# Revit family: РИДАН_Соленоидный клапан EV220WR
name_source: partatom
category: Арматура трубопроводов
units: mm (PartAtom-declared; Revit-internal decimal feet)

## family parameters
Всегда вертикально = Да
На основе рабочей плоскости = Нет
Общий = Нет
При загрузке вырезать с полостями = Нет
Размер круглого соединителя = Использовать диаметр
Тип детали = Вставляется

## types (84) — shared parameters
ADSK_Единица измерения = шт.
ADSK_Завод-изготовитель = ООО «Ридан-Трейд»
ADSK_Классификация нагрузок = Прочее
ADSK_Количество = 1
ADSK_Количество фаз = 1
ADSK_Коэффициент мощности = 1
ADSK_Потеря давления жидкости = 0.0 Па
ADSK_Расход жидкости = 0.0 л/с
LT = EV220WR _DN10_50
Table = EV220WR _DN10_50_1
angle1 = 150.00°
h2 = 69 мм

## per-type parameters (varying)
- EV220WR НЗ EPDM 0,3-16 бар 230 В 50 Гц DN10: ADSK_Диаметр условный=10 мм; ADSK_Код изделия=042U001031R; ADSK_Марка=EV220WR DN10; ADSK_Масса=0.7; ADSK_Наименование=Клапан электромагнитный EV220WR, нормально закрытый, EPDM, 0,3-16 бар, 230 В, 50 Гц, DN10; ADSK_Напряжение=230 В; ADSK_Номинальная мощность=22 Вт; ADSK_Полная мощность=22 В·А; ADSK_Пропускная способность=1.1 л/с; a=15 мм; b=15 мм; c=26 мм; d=15 мм; e=18 мм; f=36 мм; g=12 мм; h=24 мм; h1=12 мм; i=48 мм; j=4 мм; k=23 мм; l=11 мм; m=28 мм; n=16 мм; o=9 мм; p=28 мм; p1=2 мм; r=1 мм; r1=1 мм; r2=2 мм; s=38 мм; t=15 мм; t1=1 мм; u=15 мм; u1=9 мм; v=17 мм; w=77 мм; x=36 мм; x1=39 мм; x2=4 мм; x3=5 мм; y=48 мм; Ду10_40=Да; Ду50=Нет
- EV220WR НЗ EPDM 0,3-16 бар 230 В 50 Гц DN15: ADSK_Диаметр условный=15 мм; ADSK_Код изделия=042U001531R; ADSK_Марка=EV220WR DN15; ADSK_Масса=0.7; ADSK_Наименование=Клапан электромагнитный EV220WR, нормально закрытый, EPDM, 0,3-16 бар, 230 В, 50 Гц, DN15; ADSK_Напряжение=230 В; ADSK_Номинальная мощность=22 Вт; ADSK_Полная мощность=22 В·А; ADSK_Пропускная способность=1.1 л/с; a=15 мм; b=15 мм; c=26 мм; d=15 мм; e=18 мм; f=36 мм; g=12 мм; h=24 мм; h1=12 мм; i=48 мм; j=4 мм; k=23 мм; l=11 мм; m=28 мм; n=16 мм; o=9 мм; p=28 мм; p1=2 мм; r=1 мм; r1=1 мм; r2=2 мм; s=38 мм; t=15 мм; t1=1 мм; u=15 мм; u1=9 мм; v=17 мм; w=77 мм; x=36 мм; x1=39 мм; x2=4 мм; x3=5 мм; y=48 мм; Ду10_40=Да; Ду50=Нет
- EV220WR НЗ EPDM 0,3-16 бар 230 В 50 Гц DN20: ADSK_Диаметр условный=20 мм; ADSK_Код изделия=042U002031R; ADSK_Марка=EV220WR DN20; ADSK_Масса=0.85; ADSK_Наименование=Клапан электромагнитный EV220WR, нормально закрытый, EPDM, 0,3-16 бар, 230 В, 50 Гц, DN20; ADSK_Напряжение=230 В; ADSK_Номинальная мощность=22 Вт; ADSK_Полная мощность=22 В·А; ADSK_Пропускная способность=1.9 л/с; a=16 мм; b=18 мм; c=31 мм; d=20 мм; e=18 мм; f=35 мм; g=15 мм; h=29 мм; h1=14 мм; i=57 мм; j=5 мм; k=24 мм; l=11 мм; m=32 мм; n=21 мм; o=10 мм; p=30 мм; p1=2 мм; r=2 мм; r1=2 мм; r2=2 мм; s=39 мм; t=20 мм; t1=2 мм; u=24 мм; u1=9 мм; v=18 мм; w=78 мм; x=43 мм; x1=43 мм; x2=5 мм; x3=7 мм; y=57 мм; Ду10_40=Да; Ду50=Нет
- EV220WR НЗ EPDM 0,3-16 бар 230 В 50 Гц DN25: ADSK_Диаметр условный=25 мм; ADSK_Код изделия=042U002531R; ADSK_Марка=EV220WR DN25; ADSK_Масса=1.35; ADSK_Наименование=Клапан электромагнитный EV220WR, нормально закрытый, EPDM, 0,3-16 бар, 230 В, 50 Гц, DN25; ADSK_Напряжение=230 В; ADSK_Номинальная мощность=22 Вт; ADSK_Полная мощность=22 В·А; ADSK_Пропускная способность=2.8 л/с; a=23 мм; b=23 мм; c=41 мм; d=17 мм; e=31 мм; f=62 мм; g=21 мм; h=33 мм; h1=16 мм; i=70 мм; j=8 мм; k=33 мм; l=17 мм; m=40 мм; n=27 мм; o=16 мм; p=30 мм; p1=3 мм; r=13 мм; r1=2 мм; r2=3 мм; s=47 мм; t=25 мм; t1=3 мм; u=29 мм; u1=13 мм; v=28 мм; w=88 мм; x=55 мм; x1=55 мм; x2=6 мм; x3=10 мм; y=70 мм; Ду10_40=Да; Ду50=Нет
- EV220WR НЗ EPDM 0,3-16 бар 230 В 50 Гц DN32: ADSK_Диаметр условный=32 мм; ADSK_Код изделия=042U003231R; ADSK_Марка=EV220WR DN32; ADSK_Масса=2.8; ADSK_Наименование=Клапан электромагнитный EV220WR, нормально закрытый, EPDM, 0,3-16 бар, 230 В, 50 Гц, DN32; ADSK_Напряжение=230 В; ADSK_Номинальная мощность=22 Вт; ADSK_Полная мощность=22 В·А; ADSK_Пропускная способность=5.8 л/с; a=32 мм; b=31 мм; c=57 мм; d=24 мм; e=41 мм; f=83 мм; g=29 мм; h=53 мм; h1=26 мм; i=96 мм; j=12 мм; k=44 мм; l=26 мм; m=52 мм; n=40 мм; o=25 мм; p=31 мм; p1=2 мм; r=22 мм; r1=3 мм; r2=6 мм; s=59 мм; t=35 мм; t1=4 мм; u=39 мм; u1=18 мм; v=38 мм; w=98 мм; x=73 мм; x1=73 мм; x2=6 мм; x3=8 мм; y=96 мм; Ду10_40=Да; Ду50=Нет
- EV220WR НЗ EPDM 0,3-16 бар 230 В 50 Гц DN40: ADSK_Диаметр условный=40 мм; ADSK_Код изделия=042U004031R; ADSK_Марка=EV220WR DN40; ADSK_Масса=2.8; ADSK_Наименование=Клапан электромагнитный EV220WR, нормально закрытый, EPDM, 0,3-16 бар, 230 В, 50 Гц, DN40; ADSK_Напряжение=230 В; ADSK_Номинальная мощность=22 Вт; ADSK_Полная мощность=22 В·А; ADSK_Пропускная способность=7.2 л/с; a=32 мм; b=31 мм; c=57 мм; d=24 мм; e=41 мм; f=83 мм; g=29 мм; h=53 мм; h1=26 мм; i=96 мм; j=12 мм; k=44 мм; l=26 мм; m=52 мм; n=40 мм; o=25 мм; p=31 мм; p1=2 мм; r=22 мм; r1=3 мм; r2=6 мм; s=59 мм; t=35 мм; t1=4 мм; u=39 мм; u1=18 мм; v=38 мм; w=98 мм; x=73 мм; x1=73 мм; x2=6 мм; x3=8 мм; y=96 мм; Ду10_40=Да; Ду50=Нет
- EV220WR НЗ EPDM 0,3-16 бар 230 В 50 Гц DN50: ADSK_Диаметр условный=50 мм; ADSK_Код изделия=042U005031R; ADSK_Марка=EV220WR DN50; ADSK_Масса=3.9; ADSK_Наименование=Клапан электромагнитный EV220WR, нормально закрытый, EPDM, 0,3-16 бар, 230 В, 50 Гц, DN50; ADSK_Напряжение=230 В; ADSK_Номинальная мощность=22 Вт; ADSK_Полная мощность=22 В·А; ADSK_Пропускная способность=11.4 л/с; a=32 мм; b=31 мм; c=57 мм; d=33 мм; e=49 мм; f=99 мм; g=37 мм; h=56 мм; h1=28 мм; i=120 мм; j=15 мм; k=49 мм; l=31 мм; m=60 мм; n=50 мм; o=30 мм; p=40 мм; p1=3 мм; r=27 мм; r1=3 мм; r2=6 мм; s=68 мм; t=40 мм; t1=5 мм; u=39 мм; u1=18 мм; v=48 мм; w=108 мм; x=92 мм; x1=92 мм; x2=8 мм; x3=10 мм; y=130 мм; Ду10_40=Нет; Ду50=Да
- EV220WR НЗ EPDM 0,3-16 бар 24 В пост. Ток DN10: ADSK_Диаметр условный=10 мм; ADSK_Код изделия=042U001002R; ADSK_Марка=EV220WR DN10; ADSK_Масса=0.7; ADSK_Наименование=Клапан электромагнитный EV220WR, нормально закрытый, EPDM, 0,3-16 бар, 24 В пост. Ток, DN10; ADSK_Напряжение=24 В; ADSK_Номинальная мощность=13 Вт; ADSK_Полная мощность=13 В·А; ADSK_Пропускная способность=1.1 л/с; a=15 мм; b=15 мм; c=26 мм; d=15 мм; e=18 мм; f=36 мм; g=12 мм; h=24 мм; h1=12 мм; i=48 мм; j=4 мм; k=23 мм; l=11 мм; m=28 мм; n=16 мм; o=9 мм; p=28 мм; p1=2 мм; r=1 мм; r1=1 мм; r2=2 мм; s=38 мм; t=15 мм; t1=1 мм; u=15 мм; u1=9 мм; v=17 мм; w=77 мм; x=36 мм; x1=39 мм; x2=4 мм; x3=5 мм; y=48 мм; Ду10_40=Да; Ду50=Нет
- EV220WR НЗ EPDM 0,3-16 бар 24 В пост. Ток DN15: ADSK_Диаметр условный=15 мм; ADSK_Код изделия=042U001502R; ADSK_Марка=EV220WR DN15; ADSK_Масса=0.7; ADSK_Наименование=Клапан электромагнитный EV220WR, нормально закрытый, EPDM, 0,3-16 бар, 24 В пост. Ток, DN15; ADSK_Напряжение=24 В; ADSK_Номинальная мощность=13 Вт; ADSK_Полная мощность=13 В·А; ADSK_Пропускная способность=1.1 л/с; a=15 мм; b=15 мм; c=26 мм; d=15 мм; e=18 мм; f=36 мм; g=12 мм; h=24 мм; h1=12 мм; i=48 мм; j=4 мм; k=23 мм; l=11 мм; m=28 мм; n=16 мм; o=9 мм; p=28 мм; p1=2 мм; r=1 мм; r1=1 мм; r2=2 мм; s=38 мм; t=15 мм; t1=1 мм; u=15 мм; u1=9 мм; v=17 мм; w=77 мм; x=36 мм; x1=39 мм; x2=4 мм; x3=5 мм; y=48 мм; Ду10_40=Да; Ду50=Нет
- EV220WR НЗ EPDM 0,3-16 бар 24 В пост. Ток DN20: ADSK_Диаметр условный=20 мм; ADSK_Код изделия=042U002002R; ADSK_Марка=EV220WR DN20; ADSK_Масса=0.85; ADSK_Наименование=Клапан электромагнитный EV220WR, нормально закрытый, EPDM, 0,3-16 бар, 24 В пост. Ток, DN20; ADSK_Напряжение=24 В; ADSK_Номинальная мощность=13 Вт; ADSK_Полная мощность=13 В·А; ADSK_Пропускная способность=1.9 л/с; a=16 мм; b=18 мм; c=31 мм; d=20 мм; e=18 мм; f=35 мм; g=15 мм; h=29 мм; h1=14 мм; i=57 мм; j=5 мм; k=24 мм; l=11 мм; m=32 мм; n=21 мм; o=10 мм; p=30 мм; p1=2 мм; r=2 мм; r1=2 мм; r2=2 мм; s=39 мм; t=20 мм; t1=2 мм; u=24 мм; u1=9 мм; v=18 мм; w=78 мм; x=43 мм; x1=43 мм; x2=5 мм; x3=7 мм; y=57 мм; Ду10_40=Да; Ду50=Нет
- EV220WR НЗ EPDM 0,3-16 бар 24 В пост. Ток DN25: ADSK_Диаметр условный=25 мм; ADSK_Код изделия=042U002502R; ADSK_Марка=EV220WR DN25; ADSK_Масса=1.35; ADSK_Наименование=Клапан электромагнитный EV220WR, нормально закрытый, EPDM, 0,3-16 бар, 24 В пост. Ток, DN25; ADSK_Напряжение=24 В; ADSK_Номинальная мощность=13 Вт; ADSK_Полная мощность=13 В·А; ADSK_Пропускная способность=2.8 л/с; a=23 мм; b=23 мм; c=41 мм; d=17 мм; e=31 мм; f=62 мм; g=21 мм; h=33 мм; h1=16 мм; i=70 мм; j=8 мм; k=33 мм; l=17 мм; m=40 мм; n=27 мм; o=16 мм; p=30 мм; p1=3 мм; r=13 мм; r1=2 мм; r2=3 мм; s=47 мм; t=25 мм; t1=3 мм; u=29 мм; u1=13 мм; v=28 мм; w=88 мм; x=55 мм; x1=55 мм; x2=6 мм; x3=10 мм; y=70 мм; Ду10_40=Да; Ду50=Нет
- EV220WR НЗ EPDM 0,3-16 бар 24 В пост. Ток DN32: ADSK_Диаметр условный=32 мм; ADSK_Код изделия=042U003202R; ADSK_Марка=EV220WR DN32; ADSK_Масса=2.8; ADSK_Наименование=Клапан электромагнитный EV220WR, нормально закрытый, EPDM, 0,3-16 бар, 24 В пост. Ток, DN32; ADSK_Напряжение=24 В; ADSK_Номинальная мощность=13 Вт; ADSK_Полная мощность=13 В·А; ADSK_Пропускная способность=5.8 л/с; a=32 мм; b=31 мм; c=57 мм; d=24 мм; e=41 мм; f=83 мм; g=29 мм; h=53 мм; h1=26 мм; i=96 мм; j=12 мм; k=44 мм; l=26 мм; m=52 мм; n=40 мм; o=25 мм; p=31 мм; p1=2 мм; r=22 мм; r1=3 мм; r2=6 мм; s=59 мм; t=35 мм; t1=4 мм; u=39 мм; u1=18 мм; v=38 мм; w=98 мм; x=73 мм; x1=73 мм; x2=6 мм; x3=8 мм; y=96 мм; Ду10_40=Да; Ду50=Нет
- EV220WR НЗ EPDM 0,3-16 бар 24 В пост. Ток DN40: ADSK_Диаметр условный=40 мм; ADSK_Код изделия=042U004002R; ADSK_Марка=EV220WR DN40; ADSK_Масса=2.8; ADSK_Наименование=Клапан электромагнитный EV220WR, нормально закрытый, EPDM, 0,3-16 бар, 24 В пост. Ток, DN40; ADSK_Напряжение=24 В; ADSK_Номинальная мощность=13 Вт; ADSK_Полная мощность=13 В·А; ADSK_Пропускная способность=7.2 л/с; a=32 мм; b=31 мм; c=57 мм; d=24 мм; e=41 мм; f=83 мм; g=29 мм; h=53 мм; h1=26 мм; i=96 мм; j=12 мм; k=44 мм; l=26 мм; m=52 мм; n=40 мм; o=25 мм; p=31 мм; p1=2 мм; r=22 мм; r1=3 мм; r2=6 мм; s=59 мм; t=35 мм; t1=4 мм; u=39 мм; u1=18 мм; v=38 мм; w=98 мм; x=73 мм; x1=73 мм; x2=6 мм; x3=8 мм; y=96 мм; Ду10_40=Да; Ду50=Нет
- EV220WR НЗ EPDM 0,3-16 бар 24 В пост. Ток DN50: ADSK_Диаметр условный=50 мм; ADSK_Код изделия=042U005002R; ADSK_Марка=EV220WR DN50; ADSK_Масса=3.9; ADSK_Наименование=Клапан электромагнитный EV220WR, нормально закрытый, EPDM, 0,3-16 бар, 24 В пост. Ток, DN50; ADSK_Напряжение=24 В; ADSK_Номинальная мощность=13 Вт; ADSK_Полная мощность=13 В·А; ADSK_Пропускная способность=11.4 л/с; a=32 мм; b=31 мм; c=57 мм; d=33 мм; e=49 мм; f=99 мм; g=37 мм; h=56 мм; h1=28 мм; i=120 мм; j=15 мм; k=49 мм; l=31 мм; m=60 мм; n=50 мм; o=30 мм; p=40 мм; p1=3 мм; r=27 мм; r1=3 мм; r2=6 мм; s=68 мм; t=40 мм; t1=5 мм; u=39 мм; u1=18 мм; v=48 мм; w=108 мм; x=92 мм; x1=92 мм; x2=8 мм; x3=10 мм; y=130 мм; Ду10_40=Нет; Ду50=Да
- EV220WR НЗ EPDM 0,3-16 бар 24 В 50 Гц DN10: ADSK_Диаметр условный=10 мм; ADSK_Код изделия=042U001016R; ADSK_Марка=EV220WR DN10; ADSK_Масса=0.7; ADSK_Наименование=Клапан электромагнитный EV220WR, нормально закрытый, EPDM, 0,3-16 бар, 24 В, 50 Гц, DN10; ADSK_Напряжение=24 В; ADSK_Номинальная мощность=18 Вт; ADSK_Полная мощность=18 В·А; ADSK_Пропускная способность=1.1 л/с; a=15 мм; b=15 мм; c=26 мм; d=15 мм; e=18 мм; f=36 мм; g=12 мм; h=24 мм; h1=12 мм; i=48 мм; j=4 мм; k=23 мм; l=11 мм; m=28 мм; n=16 мм; o=9 мм; p=28 мм; p1=2 мм; r=1 мм; r1=1 мм; r2=2 мм; s=38 мм; t=15 мм; t1=1 мм; u=15 мм; u1=9 мм; v=17 мм; w=77 мм; x=36 мм; x1=39 мм; x2=4 мм; x3=5 мм; y=48 мм; Ду10_40=Да; Ду50=Нет
- EV220WR НЗ EPDM 0,3-16 бар 24 В 50 Гц DN15: ADSK_Диаметр условный=15 мм; ADSK_Код изделия=042U001516R; ADSK_Марка=EV220WR DN15; ADSK_Масса=0.7; ADSK_Наименование=Клапан электромагнитный EV220WR, нормально закрытый, EPDM, 0,3-16 бар, 24 В, 50 Гц, DN15; ADSK_Напряжение=24 В; ADSK_Номинальная мощность=18 Вт; ADSK_Полная мощность=18 В·А; ADSK_Пропускная способность=1.1 л/с; a=15 мм; b=15 мм; c=26 мм; d=15 мм; e=18 мм; f=36 мм; g=12 мм; h=24 мм; h1=12 мм; i=48 мм; j=4 мм; k=23 мм; l=11 мм; m=28 мм; n=16 мм; o=9 мм; p=28 мм; p1=2 мм; r=1 мм; r1=1 мм; r2=2 мм; s=38 мм; t=15 мм; t1=1 мм; u=15 мм; u1=9 мм; v=17 мм; w=77 мм; x=36 мм; x1=39 мм; x2=4 мм; x3=5 мм; y=48 мм; Ду10_40=Да; Ду50=Нет
- EV220WR НЗ EPDM 0,3-16 бар 24 В 50 Гц DN20: ADSK_Диаметр условный=20 мм; ADSK_Код изделия=042U002016R; ADSK_Марка=EV220WR DN20; ADSK_Масса=0.85; ADSK_Наименование=Клапан электромагнитный EV220WR, нормально закрытый, EPDM, 0,3-16 бар, 24 В, 50 Гц, DN20; ADSK_Напряжение=24 В; ADSK_Номинальная мощность=18 Вт; ADSK_Полная мощность=18 В·А; ADSK_Пропускная способность=1.9 л/с; a=16 мм; b=18 мм; c=31 мм; d=20 мм; e=18 мм; f=35 мм; g=15 мм; h=29 мм; h1=14 мм; i=57 мм; j=5 мм; k=24 мм; l=11 мм; m=32 мм; n=21 мм; o=10 мм; p=30 мм; p1=2 мм; r=2 мм; r1=2 мм; r2=2 мм; s=39 мм; t=20 мм; t1=2 мм; u=24 мм; u1=9 мм; v=18 мм; w=78 мм; x=43 мм; x1=43 мм; x2=5 мм; x3=7 мм; y=57 мм; Ду10_40=Да; Ду50=Нет
- EV220WR НЗ EPDM 0,3-16 бар 24 В 50 Гц DN25: ADSK_Диаметр условный=25 мм; ADSK_Код изделия=042U002516R; ADSK_Марка=EV220WR DN25; ADSK_Масса=1.35; ADSK_Наименование=Клапан электромагнитный EV220WR, нормально закрытый, EPDM, 0,3-16 бар, 24 В, 50 Гц, DN25; ADSK_Напряжение=24 В; ADSK_Номинальная мощность=18 Вт; ADSK_Полная мощность=18 В·А; ADSK_Пропускная способность=2.8 л/с; a=23 мм; b=23 мм; c=41 мм; d=17 мм; e=31 мм; f=62 мм; g=21 мм; h=33 мм; h1=16 мм; i=70 мм; j=8 мм; k=33 мм; l=17 мм; m=40 мм; n=27 мм; o=16 мм; p=30 мм; p1=3 мм; r=13 мм; r1=2 мм; r2=3 мм; s=47 мм; t=25 мм; t1=3 мм; u=29 мм; u1=13 мм; v=28 мм; w=88 мм; x=55 мм; x1=55 мм; x2=6 мм; x3=10 мм; y=70 мм; Ду10_40=Да; Ду50=Нет
- EV220WR НЗ EPDM 0,3-16 бар 24 В 50 Гц DN32: ADSK_Диаметр условный=32 мм; ADSK_Код изделия=042U003216R; ADSK_Марка=EV220WR DN32; ADSK_Масса=2.8; ADSK_Наименование=Клапан электромагнитный EV220WR, нормально закрытый, EPDM, 0,3-16 бар, 24 В, 50 Гц, DN32; ADSK_Напряжение=24 В; ADSK_Номинальная мощность=18 Вт; ADSK_Полная мощность=18 В·А; ADSK_Пропускная способность=5.8 л/с; a=32 мм; b=31 мм; c=57 мм; d=24 мм; e=41 мм; f=83 мм; g=29 мм; h=53 мм; h1=26 мм; i=96 мм; j=12 мм; k=44 мм; l=26 мм; m=52 мм; n=40 мм; o=25 мм; p=31 мм; p1=2 мм; r=22 мм; r1=3 мм; r2=6 мм; s=59 мм; t=35 мм; t1=4 мм; u=39 мм; u1=18 мм; v=38 мм; w=98 мм; x=73 мм; x1=73 мм; x2=6 мм; x3=8 мм; y=96 мм; Ду10_40=Да; Ду50=Нет
- EV220WR НЗ EPDM 0,3-16 бар 24 В 50 Гц DN40: ADSK_Диаметр условный=40 мм; ADSK_Код изделия=042U004016R; ADSK_Марка=EV220WR DN40; ADSK_Масса=2.8; ADSK_Наименование=Клапан электромагнитный EV220WR, нормально закрытый, EPDM, 0,3-16 бар, 24 В, 50 Гц, DN40; ADSK_Напряжение=24 В; ADSK_Номинальная мощность=18 Вт; ADSK_Полная мощность=18 В·А; ADSK_Пропускная способность=7.2 л/с; a=32 мм; b=31 мм; c=57 мм; d=24 мм; e=41 мм; f=83 мм; g=29 мм; h=53 мм; h1=26 мм; i=96 мм; j=12 мм; k=44 мм; l=26 мм; m=52 мм; n=40 мм; o=25 мм; p=31 мм; p1=2 мм; r=22 мм; r1=3 мм; r2=6 мм; s=59 мм; t=35 мм; t1=4 мм; u=39 мм; u1=18 мм; v=38 мм; w=98 мм; x=73 мм; x1=73 мм; x2=6 мм; x3=8 мм; y=96 мм; Ду10_40=Да; Ду50=Нет
- EV220WR НЗ EPDM 0,3-16 бар 24 В 50 Гц DN50: ADSK_Диаметр условный=50 мм; ADSK_Код изделия=042U005016R; ADSK_Марка=EV220WR DN50; ADSK_Масса=3.9; ADSK_Наименование=Клапан электромагнитный EV220WR, нормально закрытый, EPDM, 0,3-16 бар, 24 В, 50 Гц, DN50; ADSK_Напряжение=24 В; ADSK_Номинальная мощность=18 Вт; ADSK_Полная мощность=18 В·А; ADSK_Пропускная способность=11.4 л/с; a=32 мм; b=31 мм; c=57 мм; d=33 мм; e=49 мм; f=99 мм; g=37 мм; h=56 мм; h1=28 мм; i=120 мм; j=15 мм; k=49 мм; l=31 мм; m=60 мм; n=50 мм; o=30 мм; p=40 мм; p1=3 мм; r=27 мм; r1=3 мм; r2=6 мм; s=68 мм; t=40 мм; t1=5 мм; u=39 мм; u1=18 мм; v=48 мм; w=108 мм; x=92 мм; x1=92 мм; x2=8 мм; x3=10 мм; y=130 мм; Ду10_40=Нет; Ду50=Да
- EV220WR НЗ NBR 0,3-16 бар 230 В 50 Гц DN10: ADSK_Диаметр условный=10 мм; ADSK_Код изделия=042U011031R; ADSK_Марка=EV220WR DN10; ADSK_Масса=0.7; ADSK_Наименование=Клапан электромагнитный EV220WR, нормально закрытый, NBR, 0,3-16 бар, 230 В, 50 Гц, DN10; ADSK_Напряжение=230 В; ADSK_Номинальная мощность=22 Вт; ADSK_Полная мощность=22 В·А; ADSK_Пропускная способность=1.1 л/с; a=15 мм; b=15 мм; c=26 мм; d=15 мм; e=18 мм; f=36 мм; g=12 мм; h=24 мм; h1=12 мм; i=48 мм; j=4 мм; k=23 мм; l=11 мм; m=28 мм; n=16 мм; o=9 мм; p=28 мм; p1=2 мм; r=1 мм; r1=1 мм; r2=2 мм; s=38 мм; t=15 мм; t1=1 мм; u=15 мм; u1=9 мм; v=17 мм; w=77 мм; x=36 мм; x1=39 мм; x2=4 мм; x3=5 мм; y=48 мм; Ду10_40=Да; Ду50=Нет
- EV220WR НЗ NBR 0,3-16 бар 230 В 50 Гц DN15: ADSK_Диаметр условный=15 мм; ADSK_Код изделия=042U011531R; ADSK_Марка=EV220WR DN15; ADSK_Масса=0.7; ADSK_Наименование=Клапан электромагнитный EV220WR, нормально закрытый, NBR, 0,3-16 бар, 230 В, 50 Гц, DN15; ADSK_Напряжение=230 В; ADSK_Номинальная мощность=22 Вт; ADSK_Полная мощность=22 В·А; ADSK_Пропускная способность=1.1 л/с; a=15 мм; b=15 мм; c=26 мм; d=15 мм; e=18 мм; f=36 мм; g=12 мм; h=24 мм; h1=12 мм; i=48 мм; j=4 мм; k=23 мм; l=11 мм; m=28 мм; n=16 мм; o=9 мм; p=28 мм; p1=2 мм; r=1 мм; r1=1 мм; r2=2 мм; s=38 мм; t=15 мм; t1=1 мм; u=15 мм; u1=9 мм; v=17 мм; w=77 мм; x=36 мм; x1=39 мм; x2=4 мм; x3=5 мм; y=48 мм; Ду10_40=Да; Ду50=Нет
- EV220WR НЗ NBR 0,3-16 бар 230 В 50 Гц DN20: ADSK_Диаметр условный=20 мм; ADSK_Код изделия=042U012031R; ADSK_Марка=EV220WR DN20; ADSK_Масса=0.85; ADSK_Наименование=Клапан электромагнитный EV220WR, нормально закрытый, NBR, 0,3-16 бар, 230 В, 50 Гц, DN20; ADSK_Напряжение=230 В; ADSK_Номинальная мощность=22 Вт; ADSK_Полная мощность=22 В·А; ADSK_Пропускная способность=1.9 л/с; a=16 мм; b=18 мм; c=31 мм; d=20 мм; e=18 мм; f=35 мм; g=15 мм; h=29 мм; h1=14 мм; i=57 мм; j=5 мм; k=24 мм; l=11 мм; m=32 мм; n=21 мм; o=10 мм; p=30 мм; p1=2 мм; r=2 мм; r1=2 мм; r2=2 мм; s=39 мм; t=20 мм; t1=2 мм; u=24 мм; u1=9 мм; v=18 мм; w=78 мм; x=43 мм; x1=43 мм; x2=5 мм; x3=7 мм; y=57 мм; Ду10_40=Да; Ду50=Нет
- EV220WR НЗ NBR 0,3-16 бар 230 В 50 Гц DN25: ADSK_Диаметр условный=25 мм; ADSK_Код изделия=042U012531R; ADSK_Марка=EV220WR DN25; ADSK_Масса=1.35; ADSK_Наименование=Клапан электромагнитный EV220WR, нормально закрытый, NBR, 0,3-16 бар, 230 В, 50 Гц, DN25; ADSK_Напряжение=230 В; ADSK_Номинальная мощность=22 Вт; ADSK_Полная мощность=22 В·А; ADSK_Пропускная способность=2.8 л/с; a=23 мм; b=23 мм; c=41 мм; d=17 мм; e=31 мм; f=62 мм; g=21 мм; h=33 мм; h1=16 мм; i=70 мм; j=8 мм; k=33 мм; l=17 мм; m=40 мм; n=27 мм; o=16 мм; p=30 мм; p1=3 мм; r=13 мм; r1=2 мм; r2=3 мм; s=47 мм; t=25 мм; t1=3 мм; u=29 мм; u1=13 мм; v=28 мм; w=88 мм; x=55 мм; x1=55 мм; x2=6 мм; x3=10 мм; y=70 мм; Ду10_40=Да; Ду50=Нет
- EV220WR НЗ NBR 0,3-16 бар 230 В 50 Гц DN32: ADSK_Диаметр условный=32 мм; ADSK_Код изделия=042U013231R; ADSK_Марка=EV220WR DN32; ADSK_Масса=2.8; ADSK_Наименование=Клапан электромагнитный EV220WR, нормально закрытый, NBR, 0,3-16 бар, 230 В, 50 Гц, DN32; ADSK_Напряжение=230 В; ADSK_Номинальная мощность=22 Вт; ADSK_Полная мощность=22 В·А; ADSK_Пропускная способность=5.8 л/с; a=32 мм; b=31 мм; c=57 мм; d=24 мм; e=41 мм; f=83 мм; g=29 мм; h=53 мм; h1=26 мм; i=96 мм; j=12 мм; k=44 мм; l=26 мм; m=52 мм; n=40 мм; o=25 мм; p=31 мм; p1=2 мм; r=22 мм; r1=3 мм; r2=6 мм; s=59 мм; t=35 мм; t1=4 мм; u=39 мм; u1=18 мм; v=38 мм; w=98 мм; x=73 мм; x1=73 мм; x2=6 мм; x3=8 мм; y=96 мм; Ду10_40=Да; Ду50=Нет
- EV220WR НЗ NBR 0,3-16 бар 230 В 50 Гц DN40: ADSK_Диаметр условный=40 мм; ADSK_Код изделия=042U014031R; ADSK_Марка=EV220WR DN40; ADSK_Масса=2.8; ADSK_Наименование=Клапан электромагнитный EV220WR, нормально закрытый, NBR, 0,3-16 бар, 230 В, 50 Гц, DN40; ADSK_Напряжение=230 В; ADSK_Номинальная мощность=22 Вт; ADSK_Полная мощность=22 В·А; ADSK_Пропускная способность=7.2 л/с; a=32 мм; b=31 мм; c=57 мм; d=24 мм; e=41 мм; f=83 мм; g=29 мм; h=53 мм; h1=26 мм; i=96 мм; j=12 мм; k=44 мм; l=26 мм; m=52 мм; n=40 мм; o=25 мм; p=31 мм; p1=2 мм; r=22 мм; r1=3 мм; r2=6 мм; s=59 мм; t=35 мм; t1=4 мм; u=39 мм; u1=18 мм; v=38 мм; w=98 мм; x=73 мм; x1=73 мм; x2=6 мм; x3=8 мм; y=96 мм; Ду10_40=Да; Ду50=Нет
- EV220WR НЗ NBR 0,3-16 бар 230 В 50 Гц DN50: ADSK_Диаметр условный=50 мм; ADSK_Код изделия=042U015031R; ADSK_Марка=EV220WR DN50; ADSK_Масса=3.9; ADSK_Наименование=Клапан электромагнитный EV220WR, нормально закрытый, NBR, 0,3-16 бар, 230 В, 50 Гц, DN50; ADSK_Напряжение=230 В; ADSK_Номинальная мощность=22 Вт; ADSK_Полная мощность=22 В·А; ADSK_Пропускная способность=11.4 л/с; a=32 мм; b=31 мм; c=57 мм; d=33 мм; e=49 мм; f=99 мм; g=37 мм; h=56 мм; h1=28 мм; i=120 мм; j=15 мм; k=49 мм; l=31 мм; m=60 мм; n=50 мм; o=30 мм; p=40 мм; p1=3 мм; r=27 мм; r1=3 мм; r2=6 мм; s=68 мм; t=40 мм; t1=5 мм; u=39 мм; u1=18 мм; v=48 мм; w=108 мм; x=92 мм; x1=92 мм; x2=8 мм; x3=10 мм; y=130 мм; Ду10_40=Нет; Ду50=Да
- EV220WR НЗ NBR 0,3-16 бар 24 В пост. Ток DN10: ADSK_Диаметр условный=10 мм; ADSK_Код изделия=042U011002R; ADSK_Марка=EV220WR DN10; ADSK_Масса=0.7; ADSK_Наименование=Клапан электромагнитный EV220WR, нормально закрытый, NBR, 0,3-16 бар, 24 В пост. Ток, DN10; ADSK_Напряжение=24 В; ADSK_Номинальная мощность=13 Вт; ADSK_Полная мощность=13 В·А; ADSK_Пропускная способность=1.1 л/с; a=15 мм; b=15 мм; c=26 мм; d=15 мм; e=18 мм; f=36 мм; g=12 мм; h=24 мм; h1=12 мм; i=48 мм; j=4 мм; k=23 мм; l=11 мм; m=28 мм; n=16 мм; o=9 мм; p=28 мм; p1=2 мм; r=1 мм; r1=1 мм; r2=2 мм; s=38 мм; t=15 мм; t1=1 мм; u=15 мм; u1=9 мм; v=17 мм; w=77 мм; x=36 мм; x1=39 мм; x2=4 мм; x3=5 мм; y=48 мм; Ду10_40=Да; Ду50=Нет
- EV220WR НЗ NBR 0,3-16 бар 24 В пост. Ток DN15: ADSK_Диаметр условный=15 мм; ADSK_Код изделия=042U011502R; ADSK_Марка=EV220WR DN15; ADSK_Масса=0.7; ADSK_Наименование=Клапан электромагнитный EV220WR, нормально закрытый, NBR, 0,3-16 бар, 24 В пост. Ток, DN15; ADSK_Напряжение=24 В; ADSK_Номинальная мощность=13 Вт; ADSK_Полная мощность=13 В·А; ADSK_Пропускная способность=1.1 л/с; a=15 мм; b=15 мм; c=26 мм; d=15 мм; e=18 мм; f=36 мм; g=12 мм; h=24 мм; h1=12 мм; i=48 мм; j=4 мм; k=23 мм; l=11 мм; m=28 мм; n=16 мм; o=9 мм; p=28 мм; p1=2 мм; r=1 мм; r1=1 мм; r2=2 мм; s=38 мм; t=15 мм; t1=1 мм; u=15 мм; u1=9 мм; v=17 мм; w=77 мм; x=36 мм; x1=39 мм; x2=4 мм; x3=5 мм; y=48 мм; Ду10_40=Да; Ду50=Нет
- EV220WR НЗ NBR 0,3-16 бар 24 В пост. Ток DN20: ADSK_Диаметр условный=20 мм; ADSK_Код изделия=042U012002R; ADSK_Марка=EV220WR DN20; ADSK_Масса=0.85; ADSK_Наименование=Клапан электромагнитный EV220WR, нормально закрытый, NBR, 0,3-16 бар, 24 В пост. Ток, DN20; ADSK_Напряжение=24 В; ADSK_Номинальная мощность=13 Вт; ADSK_Полная мощность=13 В·А; ADSK_Пропускная способность=1.9 л/с; a=16 мм; b=18 мм; c=31 мм; d=20 мм; e=18 мм; f=35 мм; g=15 мм; h=29 мм; h1=14 мм; i=57 мм; j=5 мм; k=24 мм; l=11 мм; m=32 мм; n=21 мм; o=10 мм; p=30 мм; p1=2 мм; r=2 мм; r1=2 мм; r2=2 мм; s=39 мм; t=20 мм; t1=2 мм; u=24 мм; u1=9 мм; v=18 мм; w=78 мм; x=43 мм; x1=43 мм; x2=5 мм; x3=7 мм; y=57 мм; Ду10_40=Да; Ду50=Нет
- EV220WR НЗ NBR 0,3-16 бар 24 В пост. Ток DN25: ADSK_Диаметр условный=25 мм; ADSK_Код изделия=042U012502R; ADSK_Марка=EV220WR DN25; ADSK_Масса=1.35; ADSK_Наименование=Клапан электромагнитный EV220WR, нормально закрытый, NBR, 0,3-16 бар, 24 В пост. Ток, DN25; ADSK_Напряжение=24 В; ADSK_Номинальная мощность=13 Вт; ADSK_Полная мощность=13 В·А; ADSK_Пропускная способность=2.8 л/с; a=23 мм; b=23 мм; c=41 мм; d=17 мм; e=31 мм; f=62 мм; g=21 мм; h=33 мм; h1=16 мм; i=70 мм; j=8 мм; k=33 мм; l=17 мм; m=40 мм; n=27 мм; o=16 мм; p=30 мм; p1=3 мм; r=13 мм; r1=2 мм; r2=3 мм; s=47 мм; t=25 мм; t1=3 мм; u=29 мм; u1=13 мм; v=28 мм; w=88 мм; x=55 мм; x1=55 мм; x2=6 мм; x3=10 мм; y=70 мм; Ду10_40=Да; Ду50=Нет
- EV220WR НЗ NBR 0,3-16 бар 24 В пост. Ток DN32: ADSK_Диаметр условный=32 мм; ADSK_Код изделия=042U013202R; ADSK_Марка=EV220WR DN32; ADSK_Масса=2.8; ADSK_Наименование=Клапан электромагнитный EV220WR, нормально закрытый, NBR, 0,3-16 бар, 24 В пост. Ток, DN32; ADSK_Напряжение=24 В; ADSK_Номинальная мощность=13 Вт; ADSK_Полная мощность=13 В·А; ADSK_Пропускная способность=5.8 л/с; a=32 мм; b=31 мм; c=57 мм; d=24 мм; e=41 мм; f=83 мм; g=29 мм; h=53 мм; h1=26 мм; i=96 мм; j=12 мм; k=44 мм; l=26 мм; m=52 мм; n=40 мм; o=25 мм; p=31 мм; p1=2 мм; r=22 мм; r1=3 мм; r2=6 мм; s=59 мм; t=35 мм; t1=4 мм; u=39 мм; u1=18 мм; v=38 мм; w=98 мм; x=73 мм; x1=73 мм; x2=6 мм; x3=8 мм; y=96 мм; Ду10_40=Да; Ду50=Нет
- EV220WR НЗ NBR 0,3-16 бар 24 В пост. Ток DN40: ADSK_Диаметр условный=40 мм; ADSK_Код изделия=042U014002R; ADSK_Марка=EV220WR DN40; ADSK_Масса=2.8; ADSK_Наименование=Клапан электромагнитный EV220WR, нормально закрытый, NBR, 0,3-16 бар, 24 В пост. Ток, DN40; ADSK_Напряжение=24 В; ADSK_Номинальная мощность=13 Вт; ADSK_Полная мощность=13 В·А; ADSK_Пропускная способность=7.2 л/с; a=32 мм; b=31 мм; c=57 мм; d=24 мм; e=41 мм; f=83 мм; g=29 мм; h=53 мм; h1=26 мм; i=96 мм; j=12 мм; k=44 мм; l=26 мм; m=52 мм; n=40 мм; o=25 мм; p=31 мм; p1=2 мм; r=22 мм; r1=3 мм; r2=6 мм; s=59 мм; t=35 мм; t1=4 мм; u=39 мм; u1=18 мм; v=38 мм; w=98 мм; x=73 мм; x1=73 мм; x2=6 мм; x3=8 мм; y=96 мм; Ду10_40=Да; Ду50=Нет
- EV220WR НЗ NBR 0,3-16 бар 24 В пост. Ток DN50: ADSK_Диаметр условный=50 мм; ADSK_Код изделия=042U015002R; ADSK_Марка=EV220WR DN50; ADSK_Масса=3.9; ADSK_Наименование=Клапан электромагнитный EV220WR, нормально закрытый, NBR, 0,3-16 бар, 24 В пост. Ток, DN50; ADSK_Напряжение=24 В; ADSK_Номинальная мощность=13 Вт; ADSK_Полная мощность=13 В·А; ADSK_Пропускная способность=11.4 л/с; a=32 мм; b=31 мм; c=57 мм; d=33 мм; e=49 мм; f=99 мм; g=37 мм; h=56 мм; h1=28 мм; i=120 мм; j=15 мм; k=49 мм; l=31 мм; m=60 мм; n=50 мм; o=30 мм; p=40 мм; p1=3 мм; r=27 мм; r1=3 мм; r2=6 мм; s=68 мм; t=40 мм; t1=5 мм; u=39 мм; u1=18 мм; v=48 мм; w=108 мм; x=92 мм; x1=92 мм; x2=8 мм; x3=10 мм; y=130 мм; Ду10_40=Нет; Ду50=Да
- EV220WR НЗ NBR 0,3-16 бар 24 В 50 Гц DN10: ADSK_Диаметр условный=10 мм; ADSK_Код изделия=042U011016R; ADSK_Марка=EV220WR DN10; ADSK_Масса=0.7; ADSK_Наименование=Клапан электромагнитный EV220WR, нормально закрытый, NBR, 0,3-16 бар, 24 В, 50 Гц, DN10; ADSK_Напряжение=24 В; ADSK_Номинальная мощность=18 Вт; ADSK_Полная мощность=18 В·А; ADSK_Пропускная способность=1.1 л/с; a=15 мм; b=15 мм; c=26 мм; d=15 мм; e=18 мм; f=36 мм; g=12 мм; h=24 мм; h1=12 мм; i=48 мм; j=4 мм; k=23 мм; l=11 мм; m=28 мм; n=16 мм; o=9 мм; p=28 мм; p1=2 мм; r=1 мм; r1=1 мм; r2=2 мм; s=38 мм; t=15 мм; t1=1 мм; u=15 мм; u1=9 мм; v=17 мм; w=77 мм; x=36 мм; x1=39 мм; x2=4 мм; x3=5 мм; y=48 мм; Ду10_40=Да; Ду50=Нет
- EV220WR НЗ NBR 0,3-16 бар 24 В 50 Гц DN15: ADSK_Диаметр условный=15 мм; ADSK_Код изделия=042U011516R; ADSK_Марка=EV220WR DN15; ADSK_Масса=0.7; ADSK_Наименование=Клапан электромагнитный EV220WR, нормально закрытый, NBR, 0,3-16 бар, 24 В, 50 Гц, DN15; ADSK_Напряжение=24 В; ADSK_Номинальная мощность=18 Вт; ADSK_Полная мощность=18 В·А; ADSK_Пропускная способность=1.1 л/с; a=15 мм; b=15 мм; c=26 мм; d=15 мм; e=18 мм; f=36 мм; g=12 мм; h=24 мм; h1=12 мм; i=48 мм; j=4 мм; k=23 мм; l=11 мм; m=28 мм; n=16 мм; o=9 мм; p=28 мм; p1=2 мм; r=1 мм; r1=1 мм; r2=2 мм; s=38 мм; t=15 мм; t1=1 мм; u=15 мм; u1=9 мм; v=17 мм; w=77 мм; x=36 мм; x1=39 мм; x2=4 мм; x3=5 мм; y=48 мм; Ду10_40=Да; Ду50=Нет
- EV220WR НЗ NBR 0,3-16 бар 24 В 50 Гц DN20: ADSK_Диаметр условный=20 мм; ADSK_Код изделия=042U012016R; ADSK_Марка=EV220WR DN20; ADSK_Масса=0.85; ADSK_Наименование=Клапан электромагнитный EV220WR, нормально закрытый, NBR, 0,3-16 бар, 24 В, 50 Гц, DN20; ADSK_Напряжение=24 В; ADSK_Номинальная мощность=18 Вт; ADSK_Полная мощность=18 В·А; ADSK_Пропускная способность=1.9 л/с; a=16 мм; b=18 мм; c=31 мм; d=20 мм; e=18 мм; f=35 мм; g=15 мм; h=29 мм; h1=14 мм; i=57 мм; j=5 мм; k=24 мм; l=11 мм; m=32 мм; n=21 мм; o=10 мм; p=30 мм; p1=2 мм; r=2 мм; r1=2 мм; r2=2 мм; s=39 мм; t=20 мм; t1=2 мм; u=24 мм; u1=9 мм; v=18 мм; w=78 мм; x=43 мм; x1=43 мм; x2=5 мм; x3=7 мм; y=57 мм; Ду10_40=Да; Ду50=Нет
- EV220WR НЗ NBR 0,3-16 бар 24 В 50 Гц DN25: ADSK_Диаметр условный=25 мм; ADSK_Код изделия=042U012516R; ADSK_Марка=EV220WR DN25; ADSK_Масса=1.35; ADSK_Наименование=Клапан электромагнитный EV220WR, нормально закрытый, NBR, 0,3-16 бар, 24 В, 50 Гц, DN25; ADSK_Напряжение=24 В; ADSK_Номинальная мощность=18 Вт; ADSK_Полная мощность=18 В·А; ADSK_Пропускная способность=2.8 л/с; a=23 мм; b=23 мм; c=41 мм; d=17 мм; e=31 мм; f=62 мм; g=21 мм; h=33 мм; h1=16 мм; i=70 мм; j=8 мм; k=33 мм; l=17 мм; m=40 мм; n=27 мм; o=16 мм; p=30 мм; p1=3 мм; r=13 мм; r1=2 мм; r2=3 мм; s=47 мм; t=25 мм; t1=3 мм; u=29 мм; u1=13 мм; v=28 мм; w=88 мм; x=55 мм; x1=55 мм; x2=6 мм; x3=10 мм; y=70 мм; Ду10_40=Да; Ду50=Нет
- EV220WR НЗ NBR 0,3-16 бар 24 В 50 Гц DN32: ADSK_Диаметр условный=32 мм; ADSK_Код изделия=042U013216R; ADSK_Марка=EV220WR DN32; ADSK_Масса=2.8; ADSK_Наименование=Клапан электромагнитный EV220WR, нормально закрытый, NBR, 0,3-16 бар, 24 В, 50 Гц, DN32; ADSK_Напряжение=24 В; ADSK_Номинальная мощность=18 Вт; ADSK_Полная мощность=18 В·А; ADSK_Пропускная способность=5.8 л/с; a=32 мм; b=31 мм; c=57 мм; d=24 мм; e=41 мм; f=83 мм; g=29 мм; h=53 мм; h1=26 мм; i=96 мм; j=12 мм; k=44 мм; l=26 мм; m=52 мм; n=40 мм; o=25 мм; p=31 мм; p1=2 мм; r=22 мм; r1=3 мм; r2=6 мм; s=59 мм; t=35 мм; t1=4 мм; u=39 мм; u1=18 мм; v=38 мм; w=98 мм; x=73 мм; x1=73 мм; x2=6 мм; x3=8 мм; y=96 мм; Ду10_40=Да; Ду50=Нет
- EV220WR НЗ NBR 0,3-16 бар 24 В 50 Гц DN40: ADSK_Диаметр условный=40 мм; ADSK_Код изделия=042U014016R; ADSK_Марка=EV220WR DN40; ADSK_Масса=2.8; ADSK_Наименование=Клапан электромагнитный EV220WR, нормально закрытый, NBR, 0,3-16 бар, 24 В, 50 Гц, DN40; ADSK_Напряжение=24 В; ADSK_Номинальная мощность=18 Вт; ADSK_Полная мощность=18 В·А; ADSK_Пропускная способность=7.2 л/с; a=32 мм; b=31 мм; c=57 мм; d=24 мм; e=41 мм; f=83 мм; g=29 мм; h=53 мм; h1=26 мм; i=96 мм; j=12 мм; k=44 мм; l=26 мм; m=52 мм; n=40 мм; o=25 мм; p=31 мм; p1=2 мм; r=22 мм; r1=3 мм; r2=6 мм; s=59 мм; t=35 мм; t1=4 мм; u=39 мм; u1=18 мм; v=38 мм; w=98 мм; x=73 мм; x1=73 мм; x2=6 мм; x3=8 мм; y=96 мм; Ду10_40=Да; Ду50=Нет
- EV220WR НЗ NBR 0,3-16 бар 24 В 50 Гц DN50: ADSK_Диаметр условный=50 мм; ADSK_Код изделия=042U015016R; ADSK_Марка=EV220WR DN50; ADSK_Масса=3.9; ADSK_Наименование=Клапан электромагнитный EV220WR, нормально закрытый, NBR, 0,3-16 бар, 24 В, 50 Гц, DN50; ADSK_Напряжение=24 В; ADSK_Номинальная мощность=18 Вт; ADSK_Полная мощность=18 В·А; ADSK_Пропускная способность=11.4 л/с; a=32 мм; b=31 мм; c=57 мм; d=33 мм; e=49 мм; f=99 мм; g=37 мм; h=56 мм; h1=28 мм; i=120 мм; j=15 мм; k=49 мм; l=31 мм; m=60 мм; n=50 мм; o=30 мм; p=40 мм; p1=3 мм; r=27 мм; r1=3 мм; r2=6 мм; s=68 мм; t=40 мм; t1=5 мм; u=39 мм; u1=18 мм; v=48 мм; w=108 мм; x=92 мм; x1=92 мм; x2=8 мм; x3=10 мм; y=130 мм; Ду10_40=Нет; Ду50=Да
- EV220WR НО EPDM 0,3-13 бар 230 В 50 Гц DN10: ADSK_Диаметр условный=10 мм; ADSK_Код изделия=042U401031R; ADSK_Марка=EV220WR DN10; ADSK_Масса=0.7; ADSK_Наименование=Клапан электромагнитный EV220WR, нормально открытый, EPDM, 0,3-13 бар, 230 В, 50 Гц, DN10; ADSK_Напряжение=230 В; ADSK_Номинальная мощность=22 Вт; ADSK_Полная мощность=22 В·А; ADSK_Пропускная способность=1.1 л/с; a=15 мм; b=15 мм; c=26 мм; d=15 мм; e=18 мм; f=36 мм; g=12 мм; h=24 мм; h1=12 мм; i=48 мм; j=4 мм; k=23 мм; l=11 мм; m=28 мм; n=16 мм; o=9 мм; p=28 мм; p1=2 мм; r=1 мм; r1=1 мм; r2=2 мм; s=38 мм; t=15 мм; t1=1 мм; u=15 мм; u1=9 мм; v=17 мм; w=77 мм; x=36 мм; x1=39 мм; x2=4 мм; x3=5 мм; y=48 мм; Ду10_40=Да; Ду50=Нет
- EV220WR НО EPDM 0,3-13 бар 230 В 50 Гц DN15: ADSK_Диаметр условный=15 мм; ADSK_Код изделия=042U401531R; ADSK_Марка=EV220WR DN15; ADSK_Масса=0.7; ADSK_Наименование=Клапан электромагнитный EV220WR, нормально открытый, EPDM, 0,3-13 бар, 230 В, 50 Гц, DN15; ADSK_Напряжение=230 В; ADSK_Номинальная мощность=22 Вт; ADSK_Полная мощность=22 В·А; ADSK_Пропускная способность=1.1 л/с; a=15 мм; b=15 мм; c=26 мм; d=15 мм; e=18 мм; f=36 мм; g=12 мм; h=24 мм; h1=12 мм; i=48 мм; j=4 мм; k=23 мм; l=11 мм; m=28 мм; n=16 мм; o=9 мм; p=28 мм; p1=2 мм; r=1 мм; r1=1 мм; r2=2 мм; s=38 мм; t=15 мм; t1=1 мм; u=15 мм; u1=9 мм; v=17 мм; w=77 мм; x=36 мм; x1=39 мм; x2=4 мм; x3=5 мм; y=48 мм; Ду10_40=Да; Ду50=Нет
- EV220WR НО EPDM 0,3-13 бар 230 В 50 Гц DN20: ADSK_Диаметр условный=20 мм; ADSK_Код изделия=042U402031R; ADSK_Марка=EV220WR DN20; ADSK_Масса=0.85; ADSK_Наименование=Клапан электромагнитный EV220WR, нормально открытый, EPDM, 0,3-13 бар, 230 В, 50 Гц, DN20; ADSK_Напряжение=230 В; ADSK_Номинальная мощность=22 Вт; ADSK_Полная мощность=22 В·А; ADSK_Пропускная способность=1.9 л/с; a=16 мм; b=18 мм; c=31 мм; d=20 мм; e=18 мм; f=35 мм; g=15 мм; h=29 мм; h1=14 мм; i=57 мм; j=5 мм; k=24 мм; l=11 мм; m=32 мм; n=21 мм; o=10 мм; p=30 мм; p1=2 мм; r=2 мм; r1=2 мм; r2=2 мм; s=39 мм; t=20 мм; t1=2 мм; u=24 мм; u1=9 мм; v=18 мм; w=78 мм; x=43 мм; x1=43 мм; x2=5 мм; x3=7 мм; y=57 мм; Ду10_40=Да; Ду50=Нет
- EV220WR НО EPDM 0,3-13 бар 230 В 50 Гц DN25: ADSK_Диаметр условный=25 мм; ADSK_Код изделия=042U402531R; ADSK_Марка=EV220WR DN25; ADSK_Масса=1.35; ADSK_Наименование=Клапан электромагнитный EV220WR, нормально открытый, EPDM, 0,3-13 бар, 230 В, 50 Гц, DN25; ADSK_Напряжение=230 В; ADSK_Номинальная мощность=22 Вт; ADSK_Полная мощность=22 В·А; ADSK_Пропускная способность=2.8 л/с; a=23 мм; b=23 мм; c=41 мм; d=17 мм; e=31 мм; f=62 мм; g=21 мм; h=33 мм; h1=16 мм; i=70 мм; j=8 мм; k=33 мм; l=17 мм; m=40 мм; n=27 мм; o=16 мм; p=30 мм; p1=3 мм; r=13 мм; r1=2 мм; r2=3 мм; s=47 мм; t=25 мм; t1=3 мм; u=29 мм; u1=13 мм; v=28 мм; w=88 мм; x=55 мм; x1=55 мм; x2=6 мм; x3=10 мм; y=70 мм; Ду10_40=Да; Ду50=Нет
- EV220WR НО EPDM 0,3-8 бар 230 В 50 Гц DN32: ADSK_Диаметр условный=32 мм; ADSK_Код изделия=042U403231R; ADSK_Марка=EV220WR DN32; ADSK_Масса=2.8; ADSK_Наименование=Клапан электромагнитный EV220WR, нормально открытый, EPDM, 0,3-8 бар, 230 В, 50 Гц, DN32; ADSK_Напряжение=230 В; ADSK_Номинальная мощность=22 Вт; ADSK_Полная мощность=22 В·А; ADSK_Пропускная способность=5.8 л/с; a=32 мм; b=31 мм; c=57 мм; d=24 мм; e=41 мм; f=83 мм; g=29 мм; h=53 мм; h1=26 мм; i=96 мм; j=12 мм; k=44 мм; l=26 мм; m=52 мм; n=40 мм; o=25 мм; p=31 мм; p1=2 мм; r=22 мм; r1=3 мм; r2=6 мм; s=59 мм; t=35 мм; t1=4 мм; u=39 мм; u1=18 мм; v=38 мм; w=98 мм; x=73 мм; x1=73 мм; x2=6 мм; x3=8 мм; y=96 мм; Ду10_40=Да; Ду50=Нет
- EV220WR НО EPDM 0,3-8 бар 230 В 50 Гц DN40: ADSK_Диаметр условный=40 мм; ADSK_Код изделия=042U404031R; ADSK_Марка=EV220WR DN40; ADSK_Масса=2.8; ADSK_Наименование=Клапан электромагнитный EV220WR, нормально открытый, EPDM, 0,3-8 бар, 230 В, 50 Гц, DN40; ADSK_Напряжение=230 В; ADSK_Номинальная мощность=22 Вт; ADSK_Полная мощность=22 В·А; ADSK_Пропускная способность=7.2 л/с; a=32 мм; b=31 мм; c=57 мм; d=24 мм; e=41 мм; f=83 мм; g=29 мм; h=53 мм; h1=26 мм; i=96 мм; j=12 мм; k=44 мм; l=26 мм; m=52 мм; n=40 мм; o=25 мм; p=31 мм; p1=2 мм; r=22 мм; r1=3 мм; r2=6 мм; s=59 мм; t=35 мм; t1=4 мм; u=39 мм; u1=18 мм; v=38 мм; w=98 мм; x=73 мм; x1=73 мм; x2=6 мм; x3=8 мм; y=96 мм; Ду10_40=Да; Ду50=Нет
- EV220WR НО EPDM 0,3-8 бар 230 В 50 Гц DN50: ADSK_Диаметр условный=50 мм; ADSK_Код изделия=042U405031R; ADSK_Марка=EV220WR DN50; ADSK_Масса=3.9; ADSK_Наименование=Клапан электромагнитный EV220WR, нормально открытый, EPDM, 0,3-8 бар, 230 В, 50 Гц, DN50; ADSK_Напряжение=230 В; ADSK_Номинальная мощность=22 Вт; ADSK_Полная мощность=22 В·А; ADSK_Пропускная способность=11.4 л/с; a=32 мм; b=31 мм; c=57 мм; d=33 мм; e=49 мм; f=99 мм; g=37 мм; h=56 мм; h1=28 мм; i=120 мм; j=15 мм; k=49 мм; l=31 мм; m=60 мм; n=50 мм; o=30 мм; p=40 мм; p1=3 мм; r=27 мм; r1=3 мм; r2=6 мм; s=68 мм; t=40 мм; t1=5 мм; u=39 мм; u1=18 мм; v=48 мм; w=108 мм; x=92 мм; x1=92 мм; x2=8 мм; x3=10 мм; y=130 мм; Ду10_40=Нет; Ду50=Да
- EV220WR НО EPDM 0,3-13 бар 24 В пост. Ток DN10: ADSK_Диаметр условный=10 мм; ADSK_Код изделия=042U401002R; ADSK_Марка=EV220WR DN10; ADSK_Масса=0.7; ADSK_Наименование=Клапан электромагнитный EV220WR, нормально открытый, EPDM, 0,3-13 бар, 24 В пост. Ток, DN10; ADSK_Напряжение=24 В; ADSK_Номинальная мощность=13 Вт; ADSK_Полная мощность=13 В·А; ADSK_Пропускная способность=1.1 л/с; a=15 мм; b=15 мм; c=26 мм; d=15 мм; e=18 мм; f=36 мм; g=12 мм; h=24 мм; h1=12 мм; i=48 мм; j=4 мм; k=23 мм; l=11 мм; m=28 мм; n=16 мм; o=9 мм; p=28 мм; p1=2 мм; r=1 мм; r1=1 мм; r2=2 мм; s=38 мм; t=15 мм; t1=1 мм; u=15 мм; u1=9 мм; v=17 мм; w=77 мм; x=36 мм; x1=39 мм; x2=4 мм; x3=5 мм; y=48 мм; Ду10_40=Да; Ду50=Нет
- EV220WR НО EPDM 0,3-13 бар 24 В пост. Ток DN15: ADSK_Диаметр условный=15 мм; ADSK_Код изделия=042U401502R; ADSK_Марка=EV220WR DN15; ADSK_Масса=0.7; ADSK_Наименование=Клапан электромагнитный EV220WR, нормально открытый, EPDM, 0,3-13 бар, 24 В пост. Ток, DN15; ADSK_Напряжение=24 В; ADSK_Номинальная мощность=13 Вт; ADSK_Полная мощность=13 В·А; ADSK_Пропускная способность=1.1 л/с; a=15 мм; b=15 мм; c=26 мм; d=15 мм; e=18 мм; f=36 мм; g=12 мм; h=24 мм; h1=12 мм; i=48 мм; j=4 мм; k=23 мм; l=11 мм; m=28 мм; n=16 мм; o=9 мм; p=28 мм; p1=2 мм; r=1 мм; r1=1 мм; r2=2 мм; s=38 мм; t=15 мм; t1=1 мм; u=15 мм; u1=9 мм; v=17 мм; w=77 мм; x=36 мм; x1=39 мм; x2=4 мм; x3=5 мм; y=48 мм; Ду10_40=Да; Ду50=Нет
- EV220WR НО EPDM 0,3-13 бар 24 В пост. Ток DN20: ADSK_Диаметр условный=20 мм; ADSK_Код изделия=042U402002R; ADSK_Марка=EV220WR DN20; ADSK_Масса=0.85; ADSK_Наименование=Клапан электромагнитный EV220WR, нормально открытый, EPDM, 0,3-13 бар, 24 В пост. Ток, DN20; ADSK_Напряжение=24 В; ADSK_Номинальная мощность=13 Вт; ADSK_Полная мощность=13 В·А; ADSK_Пропускная способность=1.9 л/с; a=16 мм; b=18 мм; c=31 мм; d=20 мм; e=18 мм; f=35 мм; g=15 мм; h=29 мм; h1=14 мм; i=57 мм; j=5 мм; k=24 мм; l=11 мм; m=32 мм; n=21 мм; o=10 мм; p=30 мм; p1=2 мм; r=2 мм; r1=2 мм; r2=2 мм; s=39 мм; t=20 мм; t1=2 мм; u=24 мм; u1=9 мм; v=18 мм; w=78 мм; x=43 мм; x1=43 мм; x2=5 мм; x3=7 мм; y=57 мм; Ду10_40=Да; Ду50=Нет
- EV220WR НО EPDM 0,3-13 бар 24 В пост. Ток DN25: ADSK_Диаметр условный=25 мм; ADSK_Код изделия=042U402502R; ADSK_Марка=EV220WR DN25; ADSK_Масса=1.35; ADSK_Наименование=Клапан электромагнитный EV220WR, нормально открытый, EPDM, 0,3-13 бар, 24 В пост. Ток, DN25; ADSK_Напряжение=24 В; ADSK_Номинальная мощность=13 Вт; ADSK_Полная мощность=13 В·А; ADSK_Пропускная способность=2.8 л/с; a=23 мм; b=23 мм; c=41 мм; d=17 мм; e=31 мм; f=62 мм; g=21 мм; h=33 мм; h1=16 мм; i=70 мм; j=8 мм; k=33 мм; l=17 мм; m=40 мм; n=27 мм; o=16 мм; p=30 мм; p1=3 мм; r=13 мм; r1=2 мм; r2=3 мм; s=47 мм; t=25 мм; t1=3 мм; u=29 мм; u1=13 мм; v=28 мм; w=88 мм; x=55 мм; x1=55 мм; x2=6 мм; x3=10 мм; y=70 мм; Ду10_40=Да; Ду50=Нет
- EV220WR НО EPDM 0,3-8 бар 24 В пост. Ток DN32: ADSK_Диаметр условный=32 мм; ADSK_Код изделия=042U403202R; ADSK_Марка=EV220WR DN32; ADSK_Масса=2.8; ADSK_Наименование=Клапан электромагнитный EV220WR, нормально открытый, EPDM, 0,3-8 бар, 24 В пост. Ток, DN32; ADSK_Напряжение=24 В; ADSK_Номинальная мощность=13 Вт; ADSK_Полная мощность=13 В·А; ADSK_Пропускная способность=5.8 л/с; a=32 мм; b=31 мм; c=57 мм; d=24 мм; e=41 мм; f=83 мм; g=29 мм; h=53 мм; h1=26 мм; i=96 мм; j=12 мм; k=44 мм; l=26 мм; m=52 мм; n=40 мм; o=25 мм; p=31 мм; p1=2 мм; r=22 мм; r1=3 мм; r2=6 мм; s=59 мм; t=35 мм; t1=4 мм; u=39 мм; u1=18 мм; v=38 мм; w=98 мм; x=73 мм; x1=73 мм; x2=6 мм; x3=8 мм; y=96 мм; Ду10_40=Да; Ду50=Нет
- EV220WR НО EPDM 0,3-8 бар 24 В пост. Ток DN40: ADSK_Диаметр условный=40 мм; ADSK_Код изделия=042U404002R; ADSK_Марка=EV220WR DN40; ADSK_Масса=2.8; ADSK_Наименование=Клапан электромагнитный EV220WR, нормально открытый, EPDM, 0,3-8 бар, 24 В пост. Ток, DN40; ADSK_Напряжение=24 В; ADSK_Номинальная мощность=13 Вт; ADSK_Полная мощность=13 В·А; ADSK_Пропускная способность=7.2 л/с; a=32 мм; b=31 мм; c=57 мм; d=24 мм; e=41 мм; f=83 мм; g=29 мм; h=53 мм; h1=26 мм; i=96 мм; j=12 мм; k=44 мм; l=26 мм; m=52 мм; n=40 мм; o=25 мм; p=31 мм; p1=2 мм; r=22 мм; r1=3 мм; r2=6 мм; s=59 мм; t=35 мм; t1=4 мм; u=39 мм; u1=18 мм; v=38 мм; w=98 мм; x=73 мм; x1=73 мм; x2=6 мм; x3=8 мм; y=96 мм; Ду10_40=Да; Ду50=Нет
- EV220WR НО EPDM 0,3-8 бар 24 В пост. Ток DN50: ADSK_Диаметр условный=50 мм; ADSK_Код изделия=042U405002R; ADSK_Марка=EV220WR DN50; ADSK_Масса=3.9; ADSK_Наименование=Клапан электромагнитный EV220WR, нормально открытый, EPDM, 0,3-8 бар, 24 В пост. Ток, DN50; ADSK_Напряжение=24 В; ADSK_Номинальная мощность=13 Вт; ADSK_Полная мощность=13 В·А; ADSK_Пропускная способность=11.4 л/с; a=32 мм; b=31 мм; c=57 мм; d=33 мм; e=49 мм; f=99 мм; g=37 мм; h=56 мм; h1=28 мм; i=120 мм; j=15 мм; k=49 мм; l=31 мм; m=60 мм; n=50 мм; o=30 мм; p=40 мм; p1=3 мм; r=27 мм; r1=3 мм; r2=6 мм; s=68 мм; t=40 мм; t1=5 мм; u=39 мм; u1=18 мм; v=48 мм; w=108 мм; x=92 мм; x1=92 мм; x2=8 мм; x3=10 мм; y=130 мм; Ду10_40=Нет; Ду50=Да
- EV220WR НО EPDM 0,3-13 бар 24 В 50 Гц DN10: ADSK_Диаметр условный=10 мм; ADSK_Код изделия=042U401016R; ADSK_Марка=EV220WR DN10; ADSK_Масса=0.7; ADSK_Наименование=Клапан электромагнитный EV220WR, нормально открытый, EPDM, 0,3-13 бар, 24 В, 50 Гц, DN10; ADSK_Напряжение=24 В; ADSK_Номинальная мощность=18 Вт; ADSK_Полная мощность=18 В·А; ADSK_Пропускная способность=1.1 л/с; a=15 мм; b=15 мм; c=26 мм; d=15 мм; e=18 мм; f=36 мм; g=12 мм; h=24 мм; h1=12 мм; i=48 мм; j=4 мм; k=23 мм; l=11 мм; m=28 мм; n=16 мм; o=9 мм; p=28 мм; p1=2 мм; r=1 мм; r1=1 мм; r2=2 мм; s=38 мм; t=15 мм; t1=1 мм; u=15 мм; u1=9 мм; v=17 мм; w=77 мм; x=36 мм; x1=39 мм; x2=4 мм; x3=5 мм; y=48 мм; Ду10_40=Да; Ду50=Нет
- EV220WR НО EPDM 0,3-13 бар 24 В 50 Гц DN15: ADSK_Диаметр условный=15 мм; ADSK_Код изделия=042U401516R; ADSK_Марка=EV220WR DN15; ADSK_Масса=0.7; ADSK_Наименование=Клапан электромагнитный EV220WR, нормально открытый, EPDM, 0,3-13 бар, 24 В, 50 Гц, DN15; ADSK_Напряжение=24 В; ADSK_Номинальная мощность=18 Вт; ADSK_Полная мощность=18 В·А; ADSK_Пропускная способность=1.1 л/с; a=15 мм; b=15 мм; c=26 мм; d=15 мм; e=18 мм; f=36 мм; g=12 мм; h=24 мм; h1=12 мм; i=48 мм; j=4 мм; k=23 мм; l=11 мм; m=28 мм; n=16 мм; o=9 мм; p=28 мм; p1=2 мм; r=1 мм; r1=1 мм; r2=2 мм; s=38 мм; t=15 мм; t1=1 мм; u=15 мм; u1=9 мм; v=17 мм; w=77 мм; x=36 мм; x1=39 мм; x2=4 мм; x3=5 мм; y=48 мм; Ду10_40=Да; Ду50=Нет
- EV220WR НО EPDM 0,3-13 бар 24 В 50 Гц DN20: ADSK_Диаметр условный=20 мм; ADSK_Код изделия=042U402016R; ADSK_Марка=EV220WR DN20; ADSK_Масса=0.85; ADSK_Наименование=Клапан электромагнитный EV220WR, нормально открытый, EPDM, 0,3-13 бар, 24 В, 50 Гц, DN20; ADSK_Напряжение=24 В; ADSK_Номинальная мощность=18 Вт; ADSK_Полная мощность=18 В·А; ADSK_Пропускная способность=1.9 л/с; a=16 мм; b=18 мм; c=31 мм; d=20 мм; e=18 мм; f=35 мм; g=15 мм; h=29 мм; h1=14 мм; i=57 мм; j=5 мм; k=24 мм; l=11 мм; m=32 мм; n=21 мм; o=10 мм; p=30 мм; p1=2 мм; r=2 мм; r1=2 мм; r2=2 мм; s=39 мм; t=20 мм; t1=2 мм; u=24 мм; u1=9 мм; v=18 мм; w=78 мм; x=43 мм; x1=43 мм; x2=5 мм; x3=7 мм; y=57 мм; Ду10_40=Да; Ду50=Нет
- EV220WR НО EPDM 0,3-13 бар 24 В 50 Гц DN25: ADSK_Диаметр условный=25 мм; ADSK_Код изделия=042U402516R; ADSK_Марка=EV220WR DN25; ADSK_Масса=1.35; ADSK_Наименование=Клапан электромагнитный EV220WR, нормально открытый, EPDM, 0,3-13 бар, 24 В, 50 Гц, DN25; ADSK_Напряжение=24 В; ADSK_Номинальная мощность=18 Вт; ADSK_Полная мощность=18 В·А; ADSK_Пропускная способность=2.8 л/с; a=23 мм; b=23 мм; c=41 мм; d=17 мм; e=31 мм; f=62 мм; g=21 мм; h=33 мм; h1=16 мм; i=70 мм; j=8 мм; k=33 мм; l=17 мм; m=40 мм; n=27 мм; o=16 мм; p=30 мм; p1=3 мм; r=13 мм; r1=2 мм; r2=3 мм; s=47 мм; t=25 мм; t1=3 мм; u=29 мм; u1=13 мм; v=28 мм; w=88 мм; x=55 мм; x1=55 мм; x2=6 мм; x3=10 мм; y=70 мм; Ду10_40=Да; Ду50=Нет
- EV220WR НО EPDM 0,3-8 бар 24 В 50 Гц DN32: ADSK_Диаметр условный=32 мм; ADSK_Код изделия=042U403216R; ADSK_Марка=EV220WR DN32; ADSK_Масса=2.8; ADSK_Наименование=Клапан электромагнитный EV220WR, нормально открытый, EPDM, 0,3-8 бар, 24 В, 50 Гц, DN32; ADSK_Напряжение=24 В; ADSK_Номинальная мощность=18 Вт; ADSK_Полная мощность=18 В·А; ADSK_Пропускная способность=5.8 л/с; a=32 мм; b=31 мм; c=57 мм; d=24 мм; e=41 мм; f=83 мм; g=29 мм; h=53 мм; h1=26 мм; i=96 мм; j=12 мм; k=44 мм; l=26 мм; m=52 мм; n=40 мм; o=25 мм; p=31 мм; p1=2 мм; r=22 мм; r1=3 мм; r2=6 мм; s=59 мм; t=35 мм; t1=4 мм; u=39 мм; u1=18 мм; v=38 мм; w=98 мм; x=73 мм; x1=73 мм; x2=6 мм; x3=8 мм; y=96 мм; Ду10_40=Да; Ду50=Нет
- EV220WR НО EPDM 0,3-8 бар 24 В 50 Гц DN40: ADSK_Диаметр условный=40 мм; ADSK_Код изделия=042U404016R; ADSK_Марка=EV220WR DN40; ADSK_Масса=2.8; ADSK_Наименование=Клапан электромагнитный EV220WR, нормально открытый, EPDM, 0,3-8 бар, 24 В, 50 Гц, DN40; ADSK_Напряжение=24 В; ADSK_Номинальная мощность=18 Вт; ADSK_Полная мощность=18 В·А; ADSK_Пропускная способность=7.2 л/с; a=32 мм; b=31 мм; c=57 мм; d=24 мм; e=41 мм; f=83 мм; g=29 мм; h=53 мм; h1=26 мм; i=96 мм; j=12 мм; k=44 мм; l=26 мм; m=52 мм; n=40 мм; o=25 мм; p=31 мм; p1=2 мм; r=22 мм; r1=3 мм; r2=6 мм; s=59 мм; t=35 мм; t1=4 мм; u=39 мм; u1=18 мм; v=38 мм; w=98 мм; x=73 мм; x1=73 мм; x2=6 мм; x3=8 мм; y=96 мм; Ду10_40=Да; Ду50=Нет
- EV220WR НО EPDM 0,3-8 бар 24 В 50 Гц DN50: ADSK_Диаметр условный=50 мм; ADSK_Код изделия=042U405016R; ADSK_Марка=EV220WR DN50; ADSK_Масса=3.9; ADSK_Наименование=Клапан электромагнитный EV220WR, нормально открытый, EPDM, 0,3-8 бар, 24 В, 50 Гц, DN50; ADSK_Напряжение=24 В; ADSK_Номинальная мощность=18 Вт; ADSK_Полная мощность=18 В·А; ADSK_Пропускная способность=11.4 л/с; a=32 мм; b=31 мм; c=57 мм; d=33 мм; e=49 мм; f=99 мм; g=37 мм; h=56 мм; h1=28 мм; i=120 мм; j=15 мм; k=49 мм; l=31 мм; m=60 мм; n=50 мм; o=30 мм; p=40 мм; p1=3 мм; r=27 мм; r1=3 мм; r2=6 мм; s=68 мм; t=40 мм; t1=5 мм; u=39 мм; u1=18 мм; v=48 мм; w=108 мм; x=92 мм; x1=92 мм; x2=8 мм; x3=10 мм; y=130 мм; Ду10_40=Нет; Ду50=Да
- EV220WR НО NBR 0,3-13 бар 230 В 50 Гц DN10: ADSK_Диаметр условный=10 мм; ADSK_Код изделия=042U411031R; ADSK_Марка=EV220WR DN10; ADSK_Масса=0.7; ADSK_Наименование=Клапан электромагнитный EV220WR, нормально открытый, NBR, 0,3-13 бар, 230 В, 50 Гц, DN10; ADSK_Напряжение=230 В; ADSK_Номинальная мощность=22 Вт; ADSK_Полная мощность=22 В·А; ADSK_Пропускная способность=1.1 л/с; a=15 мм; b=15 мм; c=26 мм; d=15 мм; e=18 мм; f=36 мм; g=12 мм; h=24 мм; h1=12 мм; i=48 мм; j=4 мм; k=23 мм; l=11 мм; m=28 мм; n=16 мм; o=9 мм; p=28 мм; p1=2 мм; r=1 мм; r1=1 мм; r2=2 мм; s=38 мм; t=15 мм; t1=1 мм; u=15 мм; u1=9 мм; v=17 мм; w=77 мм; x=36 мм; x1=39 мм; x2=4 мм; x3=5 мм; y=48 мм; Ду10_40=Да; Ду50=Нет
- EV220WR НО NBR 0,3-13 бар 230 В 50 Гц DN15: ADSK_Диаметр условный=15 мм; ADSK_Код изделия=042U411531R; ADSK_Марка=EV220WR DN15; ADSK_Масса=0.7; ADSK_Наименование=Клапан электромагнитный EV220WR, нормально открытый, NBR, 0,3-13 бар, 230 В, 50 Гц, DN15; ADSK_Напряжение=230 В; ADSK_Номинальная мощность=22 Вт; ADSK_Полная мощность=22 В·А; ADSK_Пропускная способность=1.1 л/с; a=15 мм; b=15 мм; c=26 мм; d=15 мм; e=18 мм; f=36 мм; g=12 мм; h=24 мм; h1=12 мм; i=48 мм; j=4 мм; k=23 мм; l=11 мм; m=28 мм; n=16 мм; o=9 мм; p=28 мм; p1=2 мм; r=1 мм; r1=1 мм; r2=2 мм; s=38 мм; t=15 мм; t1=1 мм; u=15 мм; u1=9 мм; v=17 мм; w=77 мм; x=36 мм; x1=39 мм; x2=4 мм; x3=5 мм; y=48 мм; Ду10_40=Да; Ду50=Нет
- EV220WR НО NBR 0,3-13 бар 230 В 50 Гц DN20: ADSK_Диаметр условный=20 мм; ADSK_Код изделия=042U412031R; ADSK_Марка=EV220WR DN20; ADSK_Масса=0.85; ADSK_Наименование=Клапан электромагнитный EV220WR, нормально открытый, NBR, 0,3-13 бар, 230 В, 50 Гц, DN20; ADSK_Напряжение=230 В; ADSK_Номинальная мощность=22 Вт; ADSK_Полная мощность=22 В·А; ADSK_Пропускная способность=1.9 л/с; a=16 мм; b=18 мм; c=31 мм; d=20 мм; e=18 мм; f=35 мм; g=15 мм; h=29 мм; h1=14 мм; i=57 мм; j=5 мм; k=24 мм; l=11 мм; m=32 мм; n=21 мм; o=10 мм; p=30 мм; p1=2 мм; r=2 мм; r1=2 мм; r2=2 мм; s=39 мм; t=20 мм; t1=2 мм; u=24 мм; u1=9 мм; v=18 мм; w=78 мм; x=43 мм; x1=43 мм; x2=5 мм; x3=7 мм; y=57 мм; Ду10_40=Да; Ду50=Нет
- EV220WR НО NBR 0,3-13 бар 230 В 50 Гц DN25: ADSK_Диаметр условный=25 мм; ADSK_Код изделия=042U412531R; ADSK_Марка=EV220WR DN25; ADSK_Масса=1.35; ADSK_Наименование=Клапан электромагнитный EV220WR, нормально открытый, NBR, 0,3-13 бар, 230 В, 50 Гц, DN25; ADSK_Напряжение=230 В; ADSK_Номинальная мощность=22 Вт; ADSK_Полная мощность=22 В·А; ADSK_Пропускная способность=2.8 л/с; a=23 мм; b=23 мм; c=41 мм; d=17 мм; e=31 мм; f=62 мм; g=21 мм; h=33 мм; h1=16 мм; i=70 мм; j=8 мм; k=33 мм; l=17 мм; m=40 мм; n=27 мм; o=16 мм; p=30 мм; p1=3 мм; r=13 мм; r1=2 мм; r2=3 мм; s=47 мм; t=25 мм; t1=3 мм; u=29 мм; u1=13 мм; v=28 мм; w=88 мм; x=55 мм; x1=55 мм; x2=6 мм; x3=10 мм; y=70 мм; Ду10_40=Да; Ду50=Нет
- EV220WR НО NBR 0,3-8 бар 230 В 50 Гц DN32: ADSK_Диаметр условный=32 мм; ADSK_Код изделия=042U413231R; ADSK_Марка=EV220WR DN32; ADSK_Масса=2.8; ADSK_Наименование=Клапан электромагнитный EV220WR, нормально открытый, NBR, 0,3-8 бар, 230 В, 50 Гц, DN32; ADSK_Напряжение=230 В; ADSK_Номинальная мощность=22 Вт; ADSK_Полная мощность=22 В·А; ADSK_Пропускная способность=5.8 л/с; a=32 мм; b=31 мм; c=57 мм; d=24 мм; e=41 мм; f=83 мм; g=29 мм; h=53 мм; h1=26 мм; i=96 мм; j=12 мм; k=44 мм; l=26 мм; m=52 мм; n=40 мм; o=25 мм; p=31 мм; p1=2 мм; r=22 мм; r1=3 мм; r2=6 мм; s=59 мм; t=35 мм; t1=4 мм; u=39 мм; u1=18 мм; v=38 мм; w=98 мм; x=73 мм; x1=73 мм; x2=6 мм; x3=8 мм; y=96 мм; Ду10_40=Да; Ду50=Нет
- EV220WR НО NBR 0,3-8 бар 230 В 50 Гц DN40: ADSK_Диаметр условный=40 мм; ADSK_Код изделия=042U414031R; ADSK_Марка=EV220WR DN40; ADSK_Масса=2.8; ADSK_Наименование=Клапан электромагнитный EV220WR, нормально открытый, NBR, 0,3-8 бар, 230 В, 50 Гц, DN40; ADSK_Напряжение=230 В; ADSK_Номинальная мощность=22 Вт; ADSK_Полная мощность=22 В·А; ADSK_Пропускная способность=7.2 л/с; a=32 мм; b=31 мм; c=57 мм; d=24 мм; e=41 мм; f=83 мм; g=29 мм; h=53 мм; h1=26 мм; i=96 мм; j=12 мм; k=44 мм; l=26 мм; m=52 мм; n=40 мм; o=25 мм; p=31 мм; p1=2 мм; r=22 мм; r1=3 мм; r2=6 мм; s=59 мм; t=35 мм; t1=4 мм; u=39 мм; u1=18 мм; v=38 мм; w=98 мм; x=73 мм; x1=73 мм; x2=6 мм; x3=8 мм; y=96 мм; Ду10_40=Да; Ду50=Нет
- EV220WR НО NBR 0,3-8 бар 230 В 50 Гц DN50: ADSK_Диаметр условный=50 мм; ADSK_Код изделия=042U415031R; ADSK_Марка=EV220WR DN50; ADSK_Масса=3.9; ADSK_Наименование=Клапан электромагнитный EV220WR, нормально открытый, NBR, 0,3-8 бар, 230 В, 50 Гц, DN50; ADSK_Напряжение=230 В; ADSK_Номинальная мощность=22 Вт; ADSK_Полная мощность=22 В·А; ADSK_Пропускная способность=11.4 л/с; a=32 мм; b=31 мм; c=57 мм; d=33 мм; e=49 мм; f=99 мм; g=37 мм; h=56 мм; h1=28 мм; i=120 мм; j=15 мм; k=49 мм; l=31 мм; m=60 мм; n=50 мм; o=30 мм; p=40 мм; p1=3 мм; r=27 мм; r1=3 мм; r2=6 мм; s=68 мм; t=40 мм; t1=5 мм; u=39 мм; u1=18 мм; v=48 мм; w=108 мм; x=92 мм; x1=92 мм; x2=8 мм; x3=10 мм; y=130 мм; Ду10_40=Нет; Ду50=Да
- EV220WR НО NBR 0,3-13 бар 24 В пост. Ток DN10: ADSK_Диаметр условный=10 мм; ADSK_Код изделия=042U411002R; ADSK_Марка=EV220WR DN10; ADSK_Масса=0.7; ADSK_Наименование=Клапан электромагнитный EV220WR, нормально открытый, NBR, 0,3-13 бар, 24 В пост. Ток, DN10; ADSK_Напряжение=24 В; ADSK_Номинальная мощность=13 Вт; ADSK_Полная мощность=13 В·А; ADSK_Пропускная способность=1.1 л/с; a=15 мм; b=15 мм; c=26 мм; d=15 мм; e=18 мм; f=36 мм; g=12 мм; h=24 мм; h1=12 мм; i=48 мм; j=4 мм; k=23 мм; l=11 мм; m=28 мм; n=16 мм; o=9 мм; p=28 мм; p1=2 мм; r=1 мм; r1=1 мм; r2=2 мм; s=38 мм; t=15 мм; t1=1 мм; u=15 мм; u1=9 мм; v=17 мм; w=77 мм; x=36 мм; x1=39 мм; x2=4 мм; x3=5 мм; y=48 мм; Ду10_40=Да; Ду50=Нет
- EV220WR НО NBR 0,3-13 бар 24 В пост. Ток DN15: ADSK_Диаметр условный=15 мм; ADSK_Код изделия=042U411502R; ADSK_Марка=EV220WR DN15; ADSK_Масса=0.7; ADSK_Наименование=Клапан электромагнитный EV220WR, нормально открытый, NBR, 0,3-13 бар, 24 В пост. Ток, DN15; ADSK_Напряжение=24 В; ADSK_Номинальная мощность=13 Вт; ADSK_Полная мощность=13 В·А; ADSK_Пропускная способность=1.1 л/с; a=15 мм; b=15 мм; c=26 мм; d=15 мм; e=18 мм; f=36 мм; g=12 мм; h=24 мм; h1=12 мм; i=48 мм; j=4 мм; k=23 мм; l=11 мм; m=28 мм; n=16 мм; o=9 мм; p=28 мм; p1=2 мм; r=1 мм; r1=1 мм; r2=2 мм; s=38 мм; t=15 мм; t1=1 мм; u=15 мм; u1=9 мм; v=17 мм; w=77 мм; x=36 мм; x1=39 мм; x2=4 мм; x3=5 мм; y=48 мм; Ду10_40=Да; Ду50=Нет
- EV220WR НО NBR 0,3-13 бар 24 В пост. Ток DN20: ADSK_Диаметр условный=20 мм; ADSK_Код изделия=042U412002R; ADSK_Марка=EV220WR DN20; ADSK_Масса=0.85; ADSK_Наименование=Клапан электромагнитный EV220WR, нормально открытый, NBR, 0,3-13 бар, 24 В пост. Ток, DN20; ADSK_Напряжение=24 В; ADSK_Номинальная мощность=13 Вт; ADSK_Полная мощность=13 В·А; ADSK_Пропускная способность=1.9 л/с; a=16 мм; b=18 мм; c=31 мм; d=20 мм; e=18 мм; f=35 мм; g=15 мм; h=29 мм; h1=14 мм; i=57 мм; j=5 мм; k=24 мм; l=11 мм; m=32 мм; n=21 мм; o=10 мм; p=30 мм; p1=2 мм; r=2 мм; r1=2 мм; r2=2 мм; s=39 мм; t=20 мм; t1=2 мм; u=24 мм; u1=9 мм; v=18 мм; w=78 мм; x=43 мм; x1=43 мм; x2=5 мм; x3=7 мм; y=57 мм; Ду10_40=Да; Ду50=Нет
- EV220WR НО NBR 0,3-13 бар 24 В пост. Ток DN25: ADSK_Диаметр условный=25 мм; ADSK_Код изделия=042U412502R; ADSK_Марка=EV220WR DN25; ADSK_Масса=1.35; ADSK_Наименование=Клапан электромагнитный EV220WR, нормально открытый, NBR, 0,3-13 бар, 24 В пост. Ток, DN25; ADSK_Напряжение=24 В; ADSK_Номинальная мощность=13 Вт; ADSK_Полная мощность=13 В·А; ADSK_Пропускная способность=2.8 л/с; a=23 мм; b=23 мм; c=41 мм; d=17 мм; e=31 мм; f=62 мм; g=21 мм; h=33 мм; h1=16 мм; i=70 мм; j=8 мм; k=33 мм; l=17 мм; m=40 мм; n=27 мм; o=16 мм; p=30 мм; p1=3 мм; r=13 мм; r1=2 мм; r2=3 мм; s=47 мм; t=25 мм; t1=3 мм; u=29 мм; u1=13 мм; v=28 мм; w=88 мм; x=55 мм; x1=55 мм; x2=6 мм; x3=10 мм; y=70 мм; Ду10_40=Да; Ду50=Нет
- EV220WR НО NBR 0,3-8 бар 24 В пост. Ток DN32: ADSK_Диаметр условный=32 мм; ADSK_Код изделия=042U413202R; ADSK_Марка=EV220WR DN32; ADSK_Масса=2.8; ADSK_Наименование=Клапан электромагнитный EV220WR, нормально открытый, NBR, 0,3-8 бар, 24 В пост. Ток, DN32; ADSK_Напряжение=24 В; ADSK_Номинальная мощность=13 Вт; ADSK_Полная мощность=13 В·А; ADSK_Пропускная способность=5.8 л/с; a=32 мм; b=31 мм; c=57 мм; d=24 мм; e=41 мм; f=83 мм; g=29 мм; h=53 мм; h1=26 мм; i=96 мм; j=12 мм; k=44 мм; l=26 мм; m=52 мм; n=40 мм; o=25 мм; p=31 мм; p1=2 мм; r=22 мм; r1=3 мм; r2=6 мм; s=59 мм; t=35 мм; t1=4 мм; u=39 мм; u1=18 мм; v=38 мм; w=98 мм; x=73 мм; x1=73 мм; x2=6 мм; x3=8 мм; y=96 мм; Ду10_40=Да; Ду50=Нет
- EV220WR НО NBR 0,3-8 бар 24 В пост. Ток DN40: ADSK_Диаметр условный=40 мм; ADSK_Код изделия=042U414002R; ADSK_Марка=EV220WR DN40; ADSK_Масса=2.8; ADSK_Наименование=Клапан электромагнитный EV220WR, нормально открытый, NBR, 0,3-8 бар, 24 В пост. Ток, DN40; ADSK_Напряжение=24 В; ADSK_Номинальная мощность=13 Вт; ADSK_Полная мощность=13 В·А; ADSK_Пропускная способность=7.2 л/с; a=32 мм; b=31 мм; c=57 мм; d=24 мм; e=41 мм; f=83 мм; g=29 мм; h=53 мм; h1=26 мм; i=96 мм; j=12 мм; k=44 мм; l=26 мм; m=52 мм; n=40 мм; o=25 мм; p=31 мм; p1=2 мм; r=22 мм; r1=3 мм; r2=6 мм; s=59 мм; t=35 мм; t1=4 мм; u=39 мм; u1=18 мм; v=38 мм; w=98 мм; x=73 мм; x1=73 мм; x2=6 мм; x3=8 мм; y=96 мм; Ду10_40=Да; Ду50=Нет
- EV220WR НО NBR 0,3-8 бар 24 В пост. Ток DN50: ADSK_Диаметр условный=50 мм; ADSK_Код изделия=042U415002R; ADSK_Марка=EV220WR DN50; ADSK_Масса=3.9; ADSK_Наименование=Клапан электромагнитный EV220WR, нормально открытый, NBR, 0,3-8 бар, 24 В пост. Ток, DN50; ADSK_Напряжение=24 В; ADSK_Номинальная мощность=13 Вт; ADSK_Полная мощность=13 В·А; ADSK_Пропускная способность=11.4 л/с; a=32 мм; b=31 мм; c=57 мм; d=33 мм; e=49 мм; f=99 мм; g=37 мм; h=56 мм; h1=28 мм; i=120 мм; j=15 мм; k=49 мм; l=31 мм; m=60 мм; n=50 мм; o=30 мм; p=40 мм; p1=3 мм; r=27 мм; r1=3 мм; r2=6 мм; s=68 мм; t=40 мм; t1=5 мм; u=39 мм; u1=18 мм; v=48 мм; w=108 мм; x=92 мм; x1=92 мм; x2=8 мм; x3=10 мм; y=130 мм; Ду10_40=Нет; Ду50=Да
- EV220WR НО NBR 0,3-13 бар 24 В 50 Гц DN10: ADSK_Диаметр условный=10 мм; ADSK_Код изделия=042U411016R; ADSK_Марка=EV220WR DN10; ADSK_Масса=0.7; ADSK_Наименование=Клапан электромагнитный EV220WR, нормально открытый, NBR, 0,3-13 бар, 24 В, 50 Гц, DN10; ADSK_Напряжение=24 В; ADSK_Номинальная мощность=18 Вт; ADSK_Полная мощность=18 В·А; ADSK_Пропускная способность=1.1 л/с; a=15 мм; b=15 мм; c=26 мм; d=15 мм; e=18 мм; f=36 мм; g=12 мм; h=24 мм; h1=12 мм; i=48 мм; j=4 мм; k=23 мм; l=11 мм; m=28 мм; n=16 мм; o=9 мм; p=28 мм; p1=2 мм; r=1 мм; r1=1 мм; r2=2 мм; s=38 мм; t=15 мм; t1=1 мм; u=15 мм; u1=9 мм; v=17 мм; w=77 мм; x=36 мм; x1=39 мм; x2=4 мм; x3=5 мм; y=48 мм; Ду10_40=Да; Ду50=Нет
- EV220WR НО NBR 0,3-13 бар 24 В 50 Гц DN15: ADSK_Диаметр условный=15 мм; ADSK_Код изделия=042U411516R; ADSK_Марка=EV220WR DN15; ADSK_Масса=0.7; ADSK_Наименование=Клапан электромагнитный EV220WR, нормально открытый, NBR, 0,3-13 бар, 24 В, 50 Гц, DN15; ADSK_Напряжение=24 В; ADSK_Номинальная мощность=18 Вт; ADSK_Полная мощность=18 В·А; ADSK_Пропускная способность=1.1 л/с; a=15 мм; b=15 мм; c=26 мм; d=15 мм; e=18 мм; f=36 мм; g=12 мм; h=24 мм; h1=12 мм; i=48 мм; j=4 мм; k=23 мм; l=11 мм; m=28 мм; n=16 мм; o=9 мм; p=28 мм; p1=2 мм; r=1 мм; r1=1 мм; r2=2 мм; s=38 мм; t=15 мм; t1=1 мм; u=15 мм; u1=9 мм; v=17 мм; w=77 мм; x=36 мм; x1=39 мм; x2=4 мм; x3=5 мм; y=48 мм; Ду10_40=Да; Ду50=Нет
- EV220WR НО NBR 0,3-13 бар 24 В 50 Гц DN20: ADSK_Диаметр условный=20 мм; ADSK_Код изделия=042U412016R; ADSK_Марка=EV220WR DN20; ADSK_Масса=0.85; ADSK_Наименование=Клапан электромагнитный EV220WR, нормально открытый, NBR, 0,3-13 бар, 24 В, 50 Гц, DN20; ADSK_Напряжение=24 В; ADSK_Номинальная мощность=18 Вт; ADSK_Полная мощность=18 В·А; ADSK_Пропускная способность=1.9 л/с; a=16 мм; b=18 мм; c=31 мм; d=20 мм; e=18 мм; f=35 мм; g=15 мм; h=29 мм; h1=14 мм; i=57 мм; j=5 мм; k=24 мм; l=11 мм; m=32 мм; n=21 мм; o=10 мм; p=30 мм; p1=2 мм; r=2 мм; r1=2 мм; r2=2 мм; s=39 мм; t=20 мм; t1=2 мм; u=24 мм; u1=9 мм; v=18 мм; w=78 мм; x=43 мм; x1=43 мм; x2=5 мм; x3=7 мм; y=57 мм; Ду10_40=Да; Ду50=Нет
- EV220WR НО NBR 0,3-13 бар 24 В 50 Гц DN25: ADSK_Диаметр условный=25 мм; ADSK_Код изделия=042U412516R; ADSK_Марка=EV220WR DN25; ADSK_Масса=1.35; ADSK_Наименование=Клапан электромагнитный EV220WR, нормально открытый, NBR, 0,3-13 бар, 24 В, 50 Гц, DN25; ADSK_Напряжение=24 В; ADSK_Номинальная мощность=18 Вт; ADSK_Полная мощность=18 В·А; ADSK_Пропускная способность=2.8 л/с; a=23 мм; b=23 мм; c=41 мм; d=17 мм; e=31 мм; f=62 мм; g=21 мм; h=33 мм; h1=16 мм; i=70 мм; j=8 мм; k=33 мм; l=17 мм; m=40 мм; n=27 мм; o=16 мм; p=30 мм; p1=3 мм; r=13 мм; r1=2 мм; r2=3 мм; s=47 мм; t=25 мм; t1=3 мм; u=29 мм; u1=13 мм; v=28 мм; w=88 мм; x=55 мм; x1=55 мм; x2=6 мм; x3=10 мм; y=70 мм; Ду10_40=Да; Ду50=Нет
- EV220WR НО NBR 0,3-8 бар 24 В 50 Гц DN32: ADSK_Диаметр условный=32 мм; ADSK_Код изделия=042U413216R; ADSK_Марка=EV220WR DN32; ADSK_Масса=2.8; ADSK_Наименование=Клапан электромагнитный EV220WR, нормально открытый, NBR, 0,3-8 бар, 24 В, 50 Гц, DN32; ADSK_Напряжение=24 В; ADSK_Номинальная мощность=18 Вт; ADSK_Полная мощность=18 В·А; ADSK_Пропускная способность=5.8 л/с; a=32 мм; b=31 мм; c=57 мм; d=24 мм; e=41 мм; f=83 мм; g=29 мм; h=53 мм; h1=26 мм; i=96 мм; j=12 мм; k=44 мм; l=26 мм; m=52 мм; n=40 мм; o=25 мм; p=31 мм; p1=2 мм; r=22 мм; r1=3 мм; r2=6 мм; s=59 мм; t=35 мм; t1=4 мм; u=39 мм; u1=18 мм; v=38 мм; w=98 мм; x=73 мм; x1=73 мм; x2=6 мм; x3=8 мм; y=96 мм; Ду10_40=Да; Ду50=Нет
- EV220WR НО NBR 0,3-8 бар 24 В 50 Гц DN40: ADSK_Диаметр условный=40 мм; ADSK_Код изделия=042U414016R; ADSK_Марка=EV220WR DN40; ADSK_Масса=2.8; ADSK_Наименование=Клапан электромагнитный EV220WR, нормально открытый, NBR, 0,3-8 бар, 24 В, 50 Гц, DN40; ADSK_Напряжение=24 В; ADSK_Номинальная мощность=18 Вт; ADSK_Полная мощность=18 В·А; ADSK_Пропускная способность=7.2 л/с; a=32 мм; b=31 мм; c=57 мм; d=24 мм; e=41 мм; f=83 мм; g=29 мм; h=53 мм; h1=26 мм; i=96 мм; j=12 мм; k=44 мм; l=26 мм; m=52 мм; n=40 мм; o=25 мм; p=31 мм; p1=2 мм; r=22 мм; r1=3 мм; r2=6 мм; s=59 мм; t=35 мм; t1=4 мм; u=39 мм; u1=18 мм; v=38 мм; w=98 мм; x=73 мм; x1=73 мм; x2=6 мм; x3=8 мм; y=96 мм; Ду10_40=Да; Ду50=Нет
- EV220WR НО NBR 0,3-8 бар 24 В 50 Гц DN50: ADSK_Диаметр условный=50 мм; ADSK_Код изделия=042U415016R; ADSK_Марка=EV220WR DN50; ADSK_Масса=3.9; ADSK_Наименование=Клапан электромагнитный EV220WR, нормально открытый, NBR, 0,3-8 бар, 24 В, 50 Гц, DN50; ADSK_Напряжение=24 В; ADSK_Номинальная мощность=18 Вт; ADSK_Полная мощность=18 В·А; ADSK_Пропускная способность=11.4 л/с; a=32 мм; b=31 мм; c=57 мм; d=33 мм; e=49 мм; f=99 мм; g=37 мм; h=56 мм; h1=28 мм; i=120 мм; j=15 мм; k=49 мм; l=31 мм; m=60 мм; n=50 мм; o=30 мм; p=40 мм; p1=3 мм; r=27 мм; r1=3 мм; r2=6 мм; s=68 мм; t=40 мм; t1=5 мм; u=39 мм; u1=18 мм; v=48 мм; w=108 мм; x=92 мм; x1=92 мм; x2=8 мм; x3=10 мм; y=130 мм; Ду10_40=Нет; Ду50=Да
